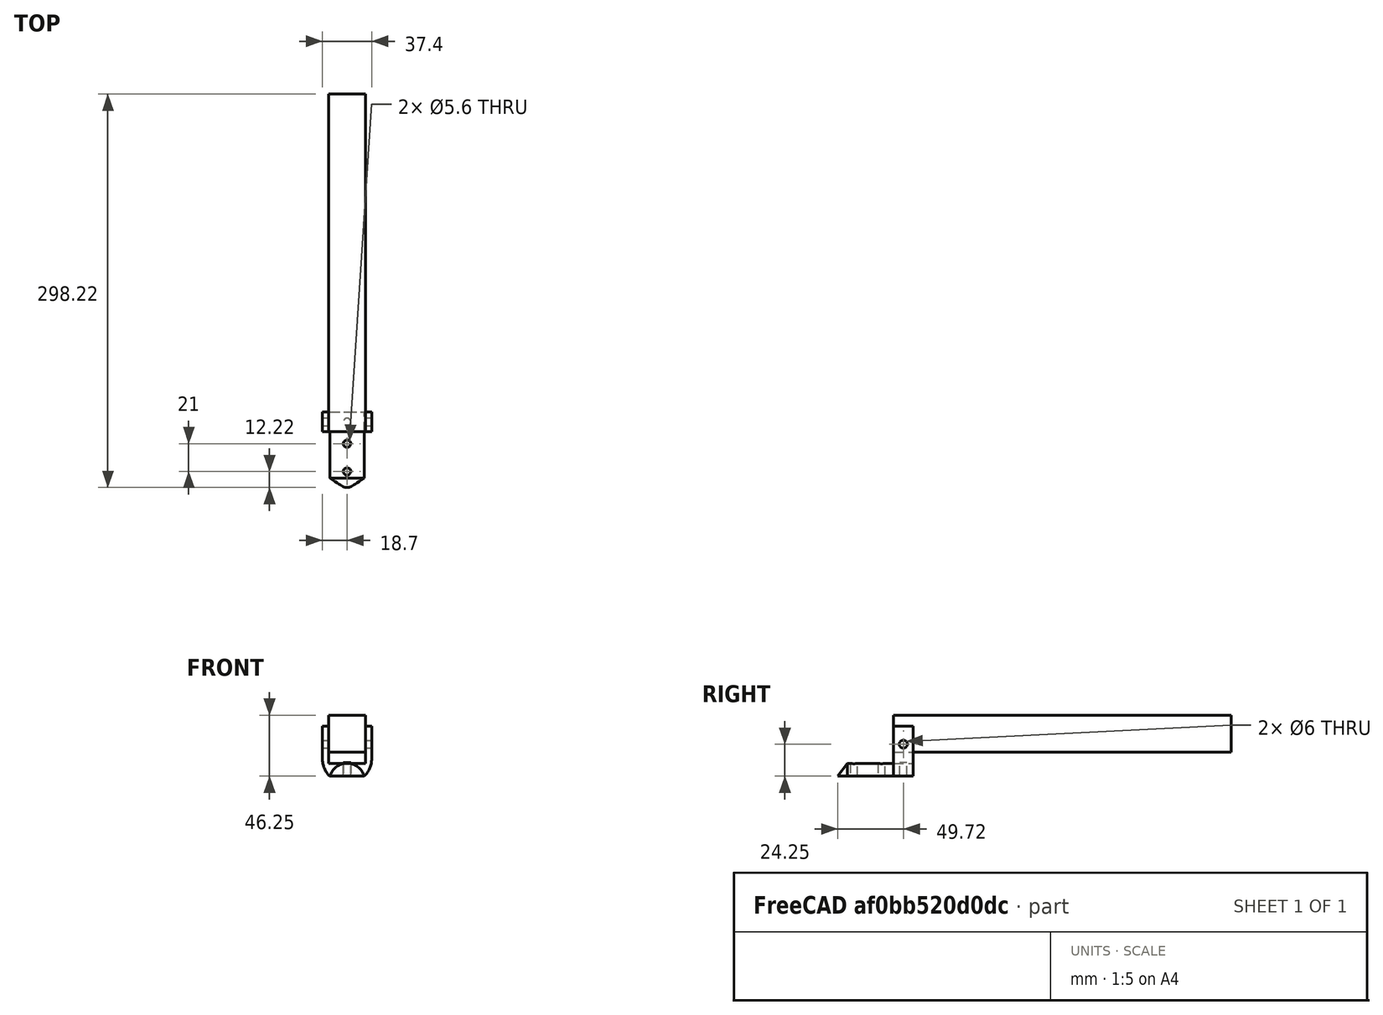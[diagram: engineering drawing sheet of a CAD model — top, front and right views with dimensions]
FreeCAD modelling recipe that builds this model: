
FCSTD DOCUMENT  (FreeCAD 0.20R29177 (Git))
Label: airModuleHolder07122022
License: All rights reserved
LicenseURL: http://en.wikipedia.org/wiki/All_rights_reserved
objects: Part::Cylinder×6, Part::Box×5, Part::Cut×4, Part::MultiFuse×4, Part::Cone×1, Part::MultiCommon×1
note: 21 computed .brp shape members not serialized (recipe doc carries the construction recipe); baked Part::Feature solids carry a one-line shape summary decoded from their .brp

FEATURE [Part::Cylinder] Cylinder
  Angle = 360
  AttacherType = Attacher::AttachEngine3D
  FirstAngle = 0
  Height = 50
  Placement = pos=(13.5,-5,43) rot=(-1,0,0;1.5708rad)
  Radius = 13.5
  SecondAngle = 0
FEATURE [Part::Box] Box  label="TSlotFrameCut"
  AttacherType = Attacher::AttachEngine3D
  Height = 28
  Length = 28
  Placement = pos=(-0.5,30,65) rot=(0,0,1;0rad)
  Width = 256
FEATURE [Part::Box] Box015  label="TSlotMount001"
  AttacherType = Attacher::AttachEngine3D
  Height = 37.75
  Length = 37.4
  Placement = pos=(-5.2,30,46.75) rot=(0,0,1;0rad)
  Width = 15
FEATURE [Part::Cylinder] Cylinder009  label="m5Cut"
  Angle = 360
  AttacherType = Attacher::AttachEngine3D
  FirstAngle = 0
  Height = 100
  Placement = pos=(-56.4,37.5,71) rot=(0,1,0;1.5708rad)
  Radius = 3
  SecondAngle = 0
FEATURE [Part::Box] Box016  label="Shell_Holder002"
  AttacherType = Attacher::AttachEngine3D
  Height = 20
  Length = 27
  Placement = pos=(0,-20.5,26.75) rot=(0,0,1;0rad)
  Width = 75
FEATURE [Part::Cylinder] Cylinder011
  Angle = 360
  AttacherType = Attacher::AttachEngine3D
  FirstAngle = 0
  Height = 12
  Placement = pos=(13.5,0,45) rot=(0,0,1;1.5708rad)
  Radius = 2.8
  SecondAngle = 0
FEATURE [Part::Cylinder] Cylinder012
  Angle = 360
  AttacherType = Attacher::AttachEngine3D
  FirstAngle = 0
  Height = 10
  Placement = pos=(13.5,37.5,47) rot=(0,0,1;1.5708rad)
  Radius = 2.8
  SecondAngle = 0
FEATURE [Part::Box] Box018  label="TSlotFrameCut001"
  AttacherType = Attacher::AttachEngine3D
  Height = 28
  Length = 28
  Placement = pos=(-0.5,0,56.5) rot=(0,0,1;0rad)
  Width = 254
FEATURE [Part::Cut] Cut009  label="TSlotMount002"
  Base = -> Box015
  Tool = -> Box018
FEATURE [Part::Cylinder] Cylinder015
  Angle = 360
  AttacherType = Attacher::AttachEngine3D
  FirstAngle = 0
  Height = 12
  Placement = pos=(13.5,21,45) rot=(0,0,1;1.5708rad)
  Radius = 2.8
  SecondAngle = 0
FEATURE [Part::Cone] Cone
  Angle = 180
  AttacherType = Attacher::AttachEngine3D
  Height = 10
  Placement = pos=(13.5,-5,43) rot=(1,0,0;1.5708rad)
  Radius1 = 13.5
  Radius2 = 0
FEATURE [Part::MultiFuse] Fusion  label="beak"
  Shapes = -> [Cylinder,Cone]
FEATURE [Part::Cut] Cut
  Base = -> Fusion
  Tool = -> Box016
FEATURE [Part::MultiFuse] Fusion001  label="heatSetCuts"
  Shapes = -> [Cylinder011,Cylinder015]
FEATURE [Part::Cut] Cut010
  Base = -> Cut009
  Tool = -> Cylinder009
FEATURE [Part::MultiFuse] Fusion002
  Shapes = -> [Cut,Cut010]
FEATURE [Part::Cut] Cut011
  Base = -> Fusion002
  Tool = -> Fusion001
FEATURE [Part::Cylinder] Cylinder016  label="reshapes"
  Angle = 360
  AttacherType = Attacher::AttachEngine3D
  FirstAngle = 0
  Height = 63
  Placement = pos=(13.5,45,60) rot=(1,0,0;1.5708rad)
  Radius = 18.7
  SecondAngle = 0
FEATURE [Part::Box] Box019  label="reshapes001"
  AttacherType = Attacher::AttachEngine3D
  Height = 29
  Length = 40
  Placement = pos=(-6.5,30,60) rot=(0,0,1;0rad)
  Width = 18
FEATURE [Part::MultiFuse] Fusion003
  Shapes = -> [Box019,Cylinder016]
FEATURE [Part::MultiCommon] Common
  Shapes = -> [Fusion003,Cut011]
